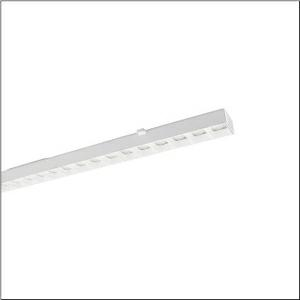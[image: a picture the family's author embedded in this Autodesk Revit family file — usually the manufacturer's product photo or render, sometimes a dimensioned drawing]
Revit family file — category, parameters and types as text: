
# Revit family: silica_31_fur_modario_31_51ry1tmb46c
name_source: partatom
category: Lighting Fixtures
units: mm (PartAtom-declared; Revit-internal decimal feet)

## family parameters
Cut with Voids When Loaded = No
Host = Face
Light Source = No
Part Type = Normal
Room Calculation Point = No
Round Connector Dimension = Use Diameter
Shared = No

## types (1)
- --- (1 x LED, 6710 lm, 37.8 W, 4000K)
    Apparent Load = 38 VA
    CIE Flux Codes = 84 98 100 100 100
    Color Rendering = 80
    Color Temperature = 4000K
    Default Elevation = 1800 mm
    Description = Silica 31 for Modario 31, luminaire insert, of aluminium, coated, traffic white (RAL 9016), length: 1.495mm, width: 79mm, height: 62mm, 5x system unit, system units: 299mm, LED rated luminous flux: 6.710lm, light colour: 840, SDCM (Standard Deviation of Colour Matching)MacAdam ≤ 3 SDCM (initial), control gear: ON/OFF Multilumen, with system connector: socket, mains connection: 220..240V, AC, 50/60Hz, rated input power: 38W, luminous flux adjustable on luminaire in four steps (3920/4730/5690/6710lm), connected load according to luminous flux setting (21.7/26.2/31.8/37.8W), primary light control with lens, of PMMA, primary anti-glare with reflector, of PC, CAT 2 (L<= 3000cd/m²), light emission: direct distribution, primary light characteristic: symmetric, protection rating (complete): IP20, insulation class (complete): insulation class I (protective earthing), certification: CE, UKCA, impact resistance: IK02, permissible ambient temperature for indoor applications: -20..+40°C, packaging unit: 1 piece
    Height = 62 mm  [stored 0.203412 ft]
    Lamp = 1 x LED
    Lamp Light Flux = 6710 lm
    Lamp Power = 37.8 W
    Lamp count = 1
    Length = 1495 mm
    Luminous efficacy = 178 lm/W
    Manufacturer = Siteco
    ModVariant = No
    Model = 51RY1TMB46C
    Mounting Place = Ceiling
    Mounting Type = Pendant
    Number of Poles = 1
    OnlyDefault = Yes
    Power Factor = 1
    Product Name = Silica 31 für Modario 31
    Product group = luminaire insert | ceiling pendant
    ProductGroupID = 901
    Protection Class = Protection class I
    Protection Degree = IP 20
    RLX_Detail_Level = 1
    RLX_Emergency_Light_Flux = 0 lm
    RLX_Emergency_Type = 0
    RLX_Emergency_Type_DB = No
    RlxData = <blob elided: 14093 chars, md5=bcfdef8f>
    Socket = socket
    Standby Power = 0 W
    System Light Flux = 6710 lm
    System Power = 38 W
    Type Comments = factory setting: luminous flux: 100 % | (OFF | OFF | OFF) | 350 mA
    Type Image = l_1299352.jpg
    URL = http://relux.com
    VarID = @adj_064613
    Voltage = 0 V
    Weight = 0.00 kg
    Width = 79 mm

note: [stored X ft] marks values corroborated as IEEE doubles in the binary element streams (Revit-internal decimal feet)

## geometry (parser evidence)
native form markers: Sweep x12
no freeform markers — native parametric forms only
